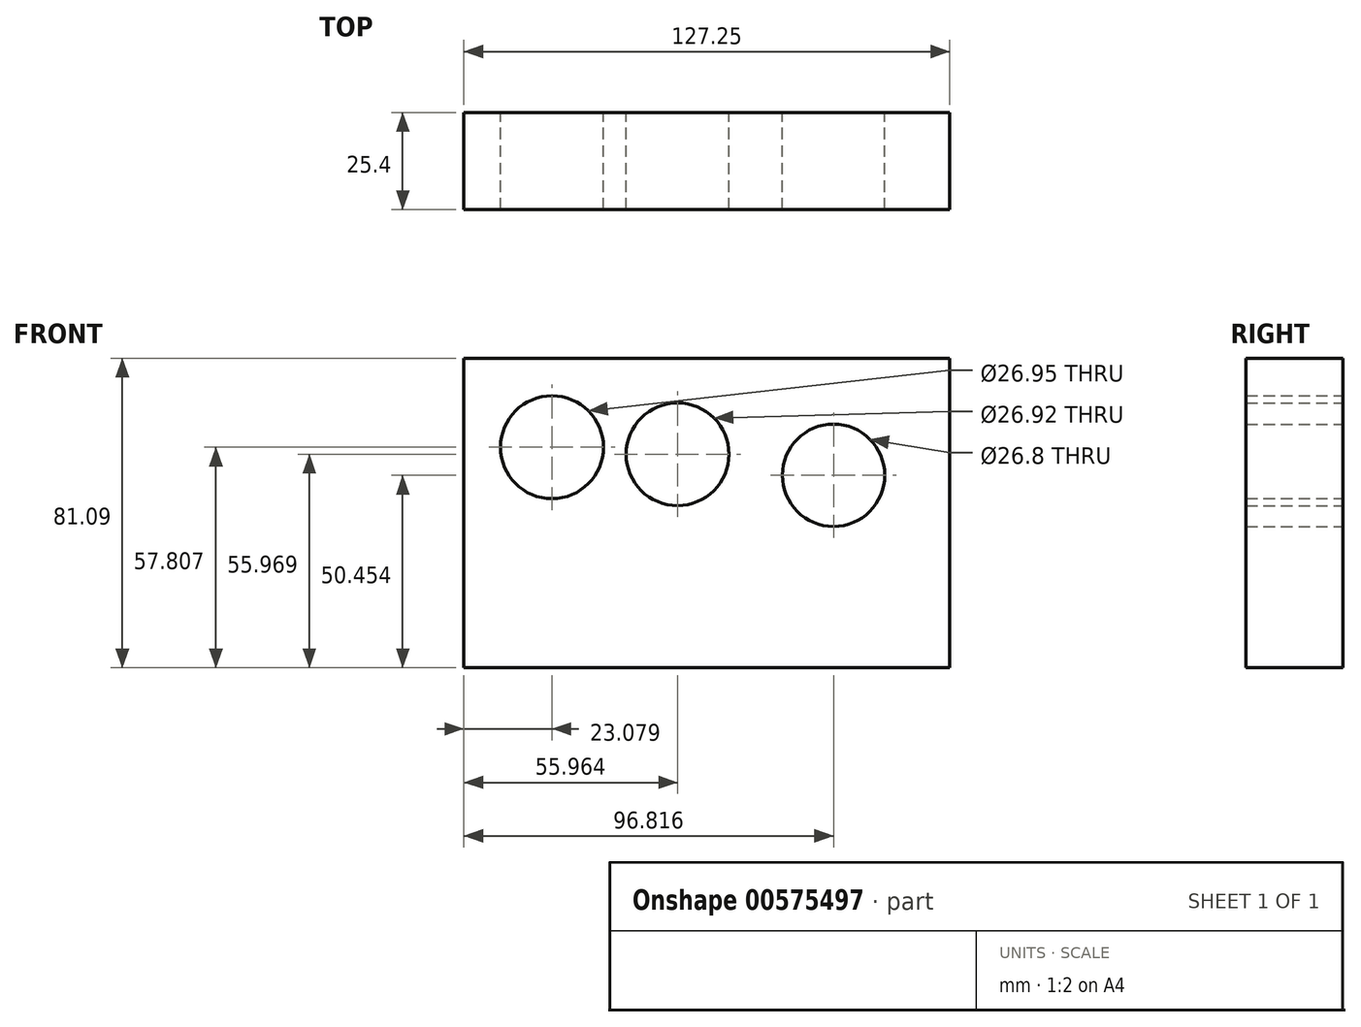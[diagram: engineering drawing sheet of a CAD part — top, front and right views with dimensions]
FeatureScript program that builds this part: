
annotation { "Feature Type Name" : "Feature", "Feature Type Description" : "" }
export const myFeature = defineFeature(function(context is Context, id is Id, definition is map)
    precondition{}
    {
        {
            var Q0;
            Q0=qCreatedBy(makeId("Front.planeOp"),FACE);
            var sketch = newSketch(context, id + "F0", { "sketchPlane" : qUnion([Q0])});
            skLineSegment(sketch, "E0.bottom", {"start": v(-68.28, 41.9) * mm, "end": v(58.97, 41.9) * mm});
            skLineSegment(sketch, "E0.top", {"start": v(-68.28, -39.2) * mm, "end": v(58.97, -39.2) * mm});
            skLineSegment(sketch, "E0.left", {"start": v(-68.28, 41.9) * mm, "end": v(-68.28, -39.2) * mm});
            skLineSegment(sketch, "E0.right", {"start": v(58.97, 41.9) * mm, "end": v(58.97, -39.2) * mm});
            skCircle(sketch, "E1", {"center": v(-45.2, 18.6) * mm, "radius": 13.47 * mm});
            skCircle(sketch, "E2", {"center": v(-12.32, 16.77) * mm, "radius": 13.46 * mm});
            skCircle(sketch, "E3", {"center": v(28.54, 11.25) * mm, "radius": 13.4 * mm});
            skSolve(sketch);
        }
        {
            var Q0;
            Q0 = qSketchRegion(id + "F0", true);
            extrude(context, id + "F1", {"entities" : qUnion([Q0]), "depth" : 25.4 * mm, "offsetDistance" : 25.4 * mm});
        }
    });
